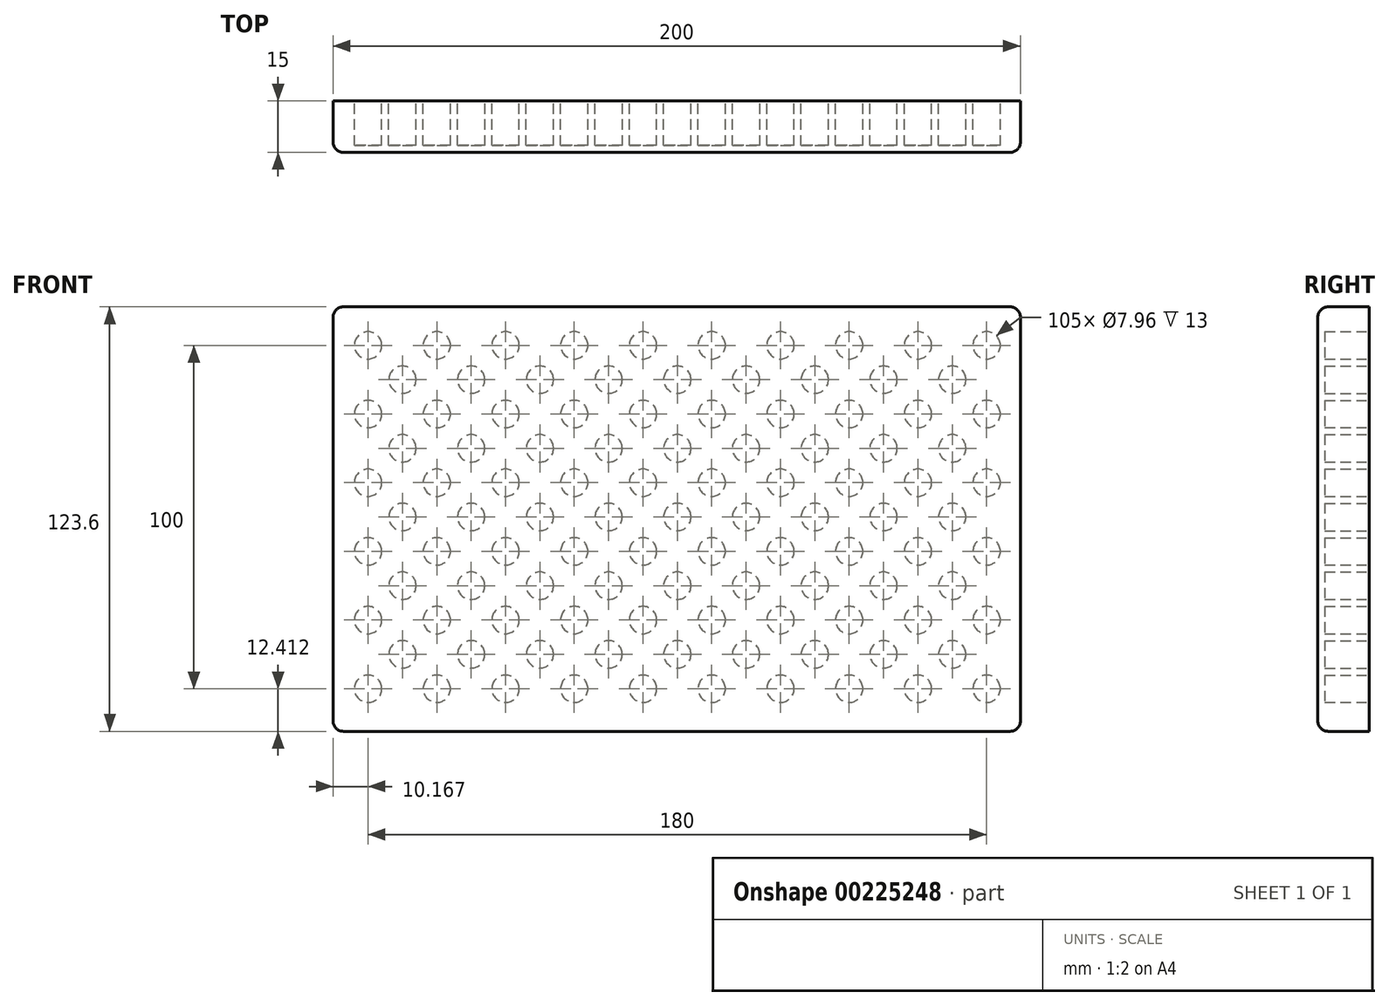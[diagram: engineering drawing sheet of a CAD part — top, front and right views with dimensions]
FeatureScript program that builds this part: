
annotation { "Feature Type Name" : "Feature", "Feature Type Description" : "" }
export const myFeature = defineFeature(function(context is Context, id is Id, definition is map)
    precondition{}
    {
        {
            var Q0;
            Q0=qCreatedBy(makeId("Front.planeOp"),FACE);
            var sketch = newSketch(context, id + "F0", { "sketchPlane" : qUnion([Q0])});
            skLineSegment(sketch, "E0.bottom", {"start": v(-100, 61.8) * mm, "end": v(23.6, 61.8) * mm});
            skLineSegment(sketch, "E0.top", {"start": v(-100, -61.8) * mm, "end": v(23.6, -61.8) * mm});
            skLineSegment(sketch, "E0.left", {"start": v(-100, 61.8) * mm, "end": v(-100, -61.8) * mm});
            skLineSegment(sketch, "E0.right", {"start": v(23.6, 61.8) * mm, "end": v(23.6, -61.8) * mm, "construction": true});
            skLineSegment(sketch, "E1", {"start": v(23.6, 61.8) * mm, "end": v(100, 61.8) * mm});
            skLineSegment(sketch, "E2", {"start": v(100, 61.8) * mm, "end": v(100, -61.8) * mm});
            skLineSegment(sketch, "E3", {"start": v(100, -61.8) * mm, "end": v(23.6, -61.8) * mm});
            skArc(sketch, "E4", {"start": v(23.6, 61.8) * mm, "mid": v(79.36, 10.85) * mm, "end": v(100, -61.8) * mm, "construction": true});
            skLineSegment(sketch, "E5", {"start": v(-38.2, -61.8) * mm, "end": v(23.6, 61.8) * mm, "construction": true});
            skSolve(sketch);
        }
        {
            var Q0;
            Q0=makeQuery(id+"F0.imprint","IMPRINT",FACE,{"disambiguationData":[TD([[makeQuery(id+"F0.imprint","IMPRINT",EDGE,{"derivedFrom":sQuery(id+"F0.wireOp",EDGE,"E0.bottom")}),-1.0]])]});
            extrude(context, id + "F1", {"entities" : qUnion([Q0]), "depth" : 15 * mm});
        }
        {
            var Q0;
            Q0=makeQuery(id+"F1.opExtrude","SWEPT_EDGE",EDGE,{"disambiguationData":[OSD([sQuery(id+"F0.wireOp",EDGE,"E0.bottom"),sQuery(id+"F0.wireOp",EDGE,"E0.left")])]});
            var Q1;
            Q1=makeQuery(id+"F1.opExtrude","SWEPT_EDGE",EDGE,{"disambiguationData":[OSD([sQuery(id+"F0.wireOp",EDGE,"E1"),sQuery(id+"F0.wireOp",EDGE,"E2")])]});
            var Q2;
            Q2=makeQuery(id+"F1.opExtrude","SWEPT_EDGE",EDGE,{"disambiguationData":[OSD([sQuery(id+"F0.wireOp",EDGE,"E0.top"),sQuery(id+"F0.wireOp",EDGE,"E0.left")])]});
            var Q3;
            Q3=makeQuery(id+"F1.opExtrude","SWEPT_EDGE",EDGE,{"disambiguationData":[OSD([sQuery(id+"F0.wireOp",EDGE,"E2"),sQuery(id+"F0.wireOp",EDGE,"E3")])]});
            var Q4;
            Q4=makeQuery(id+"F1.opExtrude","CAP_FACE",FACE,{"disambiguationData":[OSD([sQuery(id+"F0.wireOp",EDGE,"E0.bottom"),sQuery(id+"F0.wireOp",EDGE,"E0.top"),sQuery(id+"F0.wireOp",EDGE,"E0.left"),sQuery(id+"F0.wireOp",EDGE,"E1"),sQuery(id+"F0.wireOp",EDGE,"E2"),sQuery(id+"F0.wireOp",EDGE,"E3")])],"isStart":false});
            fillet(context, id + "F2", {"entities" : qUnion([Q0, Q1, Q2, Q3, Q4]), "radius" : 3 * mm, "tangentPropagation" : true, "allowEdgeOverflow" : false});
        }
        {
            var Q0;
            Q0=makeQuery(id+"F1.opExtrude","CAP_FACE",FACE,{"disambiguationData":[OSD([sQuery(id+"F0.wireOp",EDGE,"E0.bottom"),sQuery(id+"F0.wireOp",EDGE,"E0.top"),sQuery(id+"F0.wireOp",EDGE,"E0.left"),sQuery(id+"F0.wireOp",EDGE,"E1"),sQuery(id+"F0.wireOp",EDGE,"E2"),sQuery(id+"F0.wireOp",EDGE,"E3")])],"isStart":true});
            var sketch = newSketch(context, id + "F3", { "sketchPlane" : qUnion([Q0])});
            skLineSegment(sketch, "E6", {"start": v(85, 36.8) * mm, "end": v(-85, 36.8) * mm, "construction": true});
            skLineSegment(sketch, "E7", {"start": v(-65, 46.8) * mm, "end": v(-65, -46.8) * mm, "construction": true});
            skArc(sketch, "E8.0.startCap", {"start": v(85, 41.8) * mm, "mid": v(90, 36.8) * mm, "end": v(85, 31.8) * mm});
            skArc(sketch, "E8.0.endCap", {"start": v(-85, 31.8) * mm, "mid": v(-90, 36.8) * mm, "end": v(-85, 41.8) * mm});
            skLineSegment(sketch, "E8.0.left", {"start": v(85, 31.8) * mm, "end": v(-85, 31.8) * mm});
            skLineSegment(sketch, "E8.0.right", {"start": v(85, 41.8) * mm, "end": v(-85, 41.8) * mm});
            skArc(sketch, "E8.1.startCap", {"start": v(-70, 46.8) * mm, "mid": v(-65, 51.8) * mm, "end": v(-60, 46.8) * mm});
            skArc(sketch, "E8.1.endCap", {"start": v(-60, -46.8) * mm, "mid": v(-65, -51.8) * mm, "end": v(-70, -46.8) * mm});
            skLineSegment(sketch, "E8.1.left", {"start": v(-60, 46.8) * mm, "end": v(-60, -46.8) * mm});
            skLineSegment(sketch, "E8.1.right", {"start": v(-70, 46.8) * mm, "end": v(-70, -46.8) * mm});
            skSolve(sketch);
        }
        {
            var Q0;
            Q0=makeQuery(id+"F1.opExtrude","CAP_FACE",FACE,{"disambiguationData":[OSD([sQuery(id+"F0.wireOp",EDGE,"E0.bottom"),sQuery(id+"F0.wireOp",EDGE,"E0.top"),sQuery(id+"F0.wireOp",EDGE,"E0.left"),sQuery(id+"F0.wireOp",EDGE,"E1"),sQuery(id+"F0.wireOp",EDGE,"E2"),sQuery(id+"F0.wireOp",EDGE,"E3")])],"isStart":true});
            var sketch = newSketch(context, id + "F4", { "sketchPlane" : qUnion([Q0])});
            skLineSegment(sketch, "E9", {"start": v(75, 46.8) * mm, "end": v(-75, 46.8) * mm});
            skLineSegment(sketch, "E10", {"start": v(-85, 36.8) * mm, "end": v(-85, -36.8) * mm});
            skLineSegment(sketch, "E11", {"start": v(-75, -46.8) * mm, "end": v(-71, -46.8) * mm});
            skLineSegment(sketch, "E12", {"start": v(-61, -36.8) * mm, "end": v(-61, 22.8) * mm});
            skLineSegment(sketch, "E13", {"start": v(-61, 22.8) * mm, "end": v(75, 22.8) * mm});
            skLineSegment(sketch, "E14", {"start": v(85, 32.8) * mm, "end": v(85, 36.8) * mm});
            skLineSegment(sketch, "E15", {"start": v(85, 46.8) * mm, "end": v(100, 46.8) * mm, "construction": true});
            skLineSegment(sketch, "E16", {"start": v(-85, 46.8) * mm, "end": v(-85, 61.8) * mm, "construction": true});
            skLineSegment(sketch, "E17", {"start": v(-85, -46.8) * mm, "end": v(-85, -61.8) * mm, "construction": true});
            skLineSegment(sketch, "E18", {"start": v(-85, 46.8) * mm, "end": v(-100, 46.8) * mm, "construction": true});
            skPoint(sketch, "E19.visualSharp", {"position": v(-85, 46.8) * mm});
            skArc(sketch, "E19.filletArc", {"start": v(-75, 46.8) * mm, "mid": v(-82.07, 43.87) * mm, "end": v(-85, 36.8) * mm});
            skPoint(sketch, "E20.visualSharp", {"position": v(85, 46.8) * mm});
            skArc(sketch, "E20.filletArc", {"start": v(85, 36.8) * mm, "mid": v(82.07, 43.87) * mm, "end": v(75, 46.8) * mm});
            skPoint(sketch, "E21.visualSharp", {"position": v(85, 22.8) * mm});
            skArc(sketch, "E21.filletArc", {"start": v(75, 22.8) * mm, "mid": v(82.07, 25.73) * mm, "end": v(85, 32.8) * mm});
            skPoint(sketch, "E22.visualSharp", {"position": v(-61, -46.8) * mm});
            skArc(sketch, "E22.filletArc", {"start": v(-71, -46.8) * mm, "mid": v(-63.93, -43.87) * mm, "end": v(-61, -36.8) * mm});
            skPoint(sketch, "E23.visualSharp", {"position": v(-85, -46.8) * mm});
            skArc(sketch, "E23.filletArc", {"start": v(-85, -36.8) * mm, "mid": v(-82.07, -43.87) * mm, "end": v(-75, -46.8) * mm});
            skLineSegment(sketch, "E24", {"start": v(85, 22.8) * mm, "end": v(85, 46.8) * mm, "construction": true});
            skLineSegment(sketch, "E25", {"start": v(-61, -46.8) * mm, "end": v(-85, -46.8) * mm, "construction": true});
            skSolve(sketch);
        }
        {
            var Q0;
            Q0=makeQuery(id+"F1.opExtrude","CAP_FACE",FACE,{"disambiguationData":[OSD([sQuery(id+"F0.wireOp",EDGE,"E0.bottom"),sQuery(id+"F0.wireOp",EDGE,"E0.top"),sQuery(id+"F0.wireOp",EDGE,"E0.left"),sQuery(id+"F0.wireOp",EDGE,"E1"),sQuery(id+"F0.wireOp",EDGE,"E2"),sQuery(id+"F0.wireOp",EDGE,"E3")])],"isStart":true});
            var sketch = newSketch(context, id + "F5", { "sketchPlane" : qUnion([Q0])});
            skCircle(sketch, "E26", {"center": v(-90.17, 50.61) * mm, "radius": 3.98 * mm});
            skCircle(sketch, "E27.0.1.0", {"center": v(-90.17, 30.61) * mm, "radius": 3.98 * mm});
            skCircle(sketch, "E27.0.2.0", {"center": v(-90.17, 10.61) * mm, "radius": 3.98 * mm});
            skCircle(sketch, "E27.0.3.0", {"center": v(-90.17, -9.39) * mm, "radius": 3.98 * mm});
            skCircle(sketch, "E27.0.4.0", {"center": v(-90.17, -29.39) * mm, "radius": 3.98 * mm});
            skCircle(sketch, "E27.0.5.0", {"center": v(-90.17, -49.39) * mm, "radius": 3.98 * mm});
            skCircle(sketch, "E27.1.0.0", {"center": v(-70.17, 50.61) * mm, "radius": 3.98 * mm});
            skCircle(sketch, "E27.1.1.0", {"center": v(-70.17, 30.61) * mm, "radius": 3.98 * mm});
            skCircle(sketch, "E27.1.2.0", {"center": v(-70.17, 10.61) * mm, "radius": 3.98 * mm});
            skCircle(sketch, "E27.1.3.0", {"center": v(-70.17, -9.39) * mm, "radius": 3.98 * mm});
            skCircle(sketch, "E27.1.4.0", {"center": v(-70.17, -29.39) * mm, "radius": 3.98 * mm});
            skCircle(sketch, "E27.1.5.0", {"center": v(-70.17, -49.39) * mm, "radius": 3.98 * mm});
            skCircle(sketch, "E27.2.0.0", {"center": v(-50.17, 50.61) * mm, "radius": 3.98 * mm});
            skCircle(sketch, "E27.2.1.0", {"center": v(-50.17, 30.61) * mm, "radius": 3.98 * mm});
            skCircle(sketch, "E27.2.2.0", {"center": v(-50.17, 10.61) * mm, "radius": 3.98 * mm});
            skCircle(sketch, "E27.2.3.0", {"center": v(-50.17, -9.39) * mm, "radius": 3.98 * mm});
            skCircle(sketch, "E27.2.4.0", {"center": v(-50.17, -29.39) * mm, "radius": 3.98 * mm});
            skCircle(sketch, "E27.2.5.0", {"center": v(-50.17, -49.39) * mm, "radius": 3.98 * mm});
            skCircle(sketch, "E27.3.0.0", {"center": v(-30.17, 50.61) * mm, "radius": 3.98 * mm});
            skCircle(sketch, "E27.3.1.0", {"center": v(-30.17, 30.61) * mm, "radius": 3.98 * mm});
            skCircle(sketch, "E27.3.2.0", {"center": v(-30.17, 10.61) * mm, "radius": 3.98 * mm});
            skCircle(sketch, "E27.3.3.0", {"center": v(-30.17, -9.39) * mm, "radius": 3.98 * mm});
            skCircle(sketch, "E27.3.4.0", {"center": v(-30.17, -29.39) * mm, "radius": 3.98 * mm});
            skCircle(sketch, "E27.3.5.0", {"center": v(-30.17, -49.39) * mm, "radius": 3.98 * mm});
            skCircle(sketch, "E27.4.0.0", {"center": v(-10.17, 50.61) * mm, "radius": 3.98 * mm});
            skCircle(sketch, "E27.4.1.0", {"center": v(-10.17, 30.61) * mm, "radius": 3.98 * mm});
            skCircle(sketch, "E27.4.2.0", {"center": v(-10.17, 10.61) * mm, "radius": 3.98 * mm});
            skCircle(sketch, "E27.4.3.0", {"center": v(-10.17, -9.39) * mm, "radius": 3.98 * mm});
            skCircle(sketch, "E27.4.4.0", {"center": v(-10.17, -29.39) * mm, "radius": 3.98 * mm});
            skCircle(sketch, "E27.4.5.0", {"center": v(-10.17, -49.39) * mm, "radius": 3.98 * mm});
            skCircle(sketch, "E27.5.0.0", {"center": v(9.83, 50.61) * mm, "radius": 3.98 * mm});
            skCircle(sketch, "E27.5.1.0", {"center": v(9.83, 30.61) * mm, "radius": 3.98 * mm});
            skCircle(sketch, "E27.5.2.0", {"center": v(9.83, 10.61) * mm, "radius": 3.98 * mm});
            skCircle(sketch, "E27.5.3.0", {"center": v(9.83, -9.39) * mm, "radius": 3.98 * mm});
            skCircle(sketch, "E27.5.4.0", {"center": v(9.83, -29.39) * mm, "radius": 3.98 * mm});
            skCircle(sketch, "E27.5.5.0", {"center": v(9.83, -49.39) * mm, "radius": 3.98 * mm});
            skCircle(sketch, "E27.6.0.0", {"center": v(29.83, 50.61) * mm, "radius": 3.98 * mm});
            skCircle(sketch, "E27.6.1.0", {"center": v(29.83, 30.61) * mm, "radius": 3.98 * mm});
            skCircle(sketch, "E27.6.2.0", {"center": v(29.83, 10.61) * mm, "radius": 3.98 * mm});
            skCircle(sketch, "E27.6.3.0", {"center": v(29.83, -9.39) * mm, "radius": 3.98 * mm});
            skCircle(sketch, "E27.6.4.0", {"center": v(29.83, -29.39) * mm, "radius": 3.98 * mm});
            skCircle(sketch, "E27.6.5.0", {"center": v(29.83, -49.39) * mm, "radius": 3.98 * mm});
            skCircle(sketch, "E27.7.0.0", {"center": v(49.83, 50.61) * mm, "radius": 3.98 * mm});
            skCircle(sketch, "E27.7.1.0", {"center": v(49.83, 30.61) * mm, "radius": 3.98 * mm});
            skCircle(sketch, "E27.7.2.0", {"center": v(49.83, 10.61) * mm, "radius": 3.98 * mm});
            skCircle(sketch, "E27.7.3.0", {"center": v(49.83, -9.39) * mm, "radius": 3.98 * mm});
            skCircle(sketch, "E27.7.4.0", {"center": v(49.83, -29.39) * mm, "radius": 3.98 * mm});
            skCircle(sketch, "E27.7.5.0", {"center": v(49.83, -49.39) * mm, "radius": 3.98 * mm});
            skCircle(sketch, "E27.8.0.0", {"center": v(69.83, 50.61) * mm, "radius": 3.98 * mm});
            skCircle(sketch, "E27.8.1.0", {"center": v(69.83, 30.61) * mm, "radius": 3.98 * mm});
            skCircle(sketch, "E27.8.2.0", {"center": v(69.83, 10.61) * mm, "radius": 3.98 * mm});
            skCircle(sketch, "E27.8.3.0", {"center": v(69.83, -9.39) * mm, "radius": 3.98 * mm});
            skCircle(sketch, "E27.8.4.0", {"center": v(69.83, -29.39) * mm, "radius": 3.98 * mm});
            skCircle(sketch, "E27.8.5.0", {"center": v(69.83, -49.39) * mm, "radius": 3.98 * mm});
            skCircle(sketch, "E27.9.0.0", {"center": v(89.83, 50.61) * mm, "radius": 3.98 * mm});
            skCircle(sketch, "E27.9.1.0", {"center": v(89.83, 30.61) * mm, "radius": 3.98 * mm});
            skCircle(sketch, "E27.9.2.0", {"center": v(89.83, 10.61) * mm, "radius": 3.98 * mm});
            skCircle(sketch, "E27.9.3.0", {"center": v(89.83, -9.39) * mm, "radius": 3.98 * mm});
            skCircle(sketch, "E27.9.4.0", {"center": v(89.83, -29.39) * mm, "radius": 3.98 * mm});
            skCircle(sketch, "E27.9.5.0", {"center": v(89.83, -49.39) * mm, "radius": 3.98 * mm});
            skLineSegment(sketch, "E27.direction1", {"start": v(-90.17, 50.61) * mm, "end": v(-70.17, 50.61) * mm, "construction": true});
            skLineSegment(sketch, "E27.direction2", {"start": v(-90.17, 50.61) * mm, "end": v(-90.17, 30.61) * mm, "construction": true});
            skLineSegment(sketch, "E28", {"start": v(-70.17, 30.61) * mm, "end": v(-90.17, 50.61) * mm, "construction": true});
            skCircle(sketch, "E29", {"center": v(-80.17, 40.61) * mm, "radius": 3.98 * mm});
            skCircle(sketch, "E30.0.1.0", {"center": v(-80.17, 20.61) * mm, "radius": 3.98 * mm});
            skCircle(sketch, "E30.0.2.0", {"center": v(-80.17, 0.61) * mm, "radius": 3.98 * mm});
            skCircle(sketch, "E30.0.3.0", {"center": v(-80.17, -19.39) * mm, "radius": 3.98 * mm});
            skCircle(sketch, "E30.0.4.0", {"center": v(-80.17, -39.39) * mm, "radius": 3.98 * mm});
            skCircle(sketch, "E30.1.0.0", {"center": v(-60.17, 40.61) * mm, "radius": 3.98 * mm});
            skCircle(sketch, "E30.1.1.0", {"center": v(-60.17, 20.61) * mm, "radius": 3.98 * mm});
            skCircle(sketch, "E30.1.2.0", {"center": v(-60.17, 0.61) * mm, "radius": 3.98 * mm});
            skCircle(sketch, "E30.1.3.0", {"center": v(-60.17, -19.39) * mm, "radius": 3.98 * mm});
            skCircle(sketch, "E30.1.4.0", {"center": v(-60.17, -39.39) * mm, "radius": 3.98 * mm});
            skCircle(sketch, "E30.2.0.0", {"center": v(-40.17, 40.61) * mm, "radius": 3.98 * mm});
            skCircle(sketch, "E30.2.1.0", {"center": v(-40.17, 20.61) * mm, "radius": 3.98 * mm});
            skCircle(sketch, "E30.2.2.0", {"center": v(-40.17, 0.61) * mm, "radius": 3.98 * mm});
            skCircle(sketch, "E30.2.3.0", {"center": v(-40.17, -19.39) * mm, "radius": 3.98 * mm});
            skCircle(sketch, "E30.2.4.0", {"center": v(-40.17, -39.39) * mm, "radius": 3.98 * mm});
            skCircle(sketch, "E30.3.0.0", {"center": v(-20.17, 40.61) * mm, "radius": 3.98 * mm});
            skCircle(sketch, "E30.3.1.0", {"center": v(-20.17, 20.61) * mm, "radius": 3.98 * mm});
            skCircle(sketch, "E30.3.2.0", {"center": v(-20.17, 0.61) * mm, "radius": 3.98 * mm});
            skCircle(sketch, "E30.3.3.0", {"center": v(-20.17, -19.39) * mm, "radius": 3.98 * mm});
            skCircle(sketch, "E30.3.4.0", {"center": v(-20.17, -39.39) * mm, "radius": 3.98 * mm});
            skCircle(sketch, "E30.4.0.0", {"center": v(-0.17, 40.61) * mm, "radius": 3.98 * mm});
            skCircle(sketch, "E30.4.1.0", {"center": v(-0.17, 20.61) * mm, "radius": 3.98 * mm});
            skCircle(sketch, "E30.4.2.0", {"center": v(-0.17, 0.61) * mm, "radius": 3.98 * mm});
            skCircle(sketch, "E30.4.3.0", {"center": v(-0.17, -19.39) * mm, "radius": 3.98 * mm});
            skCircle(sketch, "E30.4.4.0", {"center": v(-0.17, -39.39) * mm, "radius": 3.98 * mm});
            skCircle(sketch, "E30.5.0.0", {"center": v(19.83, 40.61) * mm, "radius": 3.98 * mm});
            skCircle(sketch, "E30.5.1.0", {"center": v(19.83, 20.61) * mm, "radius": 3.98 * mm});
            skCircle(sketch, "E30.5.2.0", {"center": v(19.83, 0.61) * mm, "radius": 3.98 * mm});
            skCircle(sketch, "E30.5.3.0", {"center": v(19.83, -19.39) * mm, "radius": 3.98 * mm});
            skCircle(sketch, "E30.5.4.0", {"center": v(19.83, -39.39) * mm, "radius": 3.98 * mm});
            skCircle(sketch, "E30.6.0.0", {"center": v(39.83, 40.61) * mm, "radius": 3.98 * mm});
            skCircle(sketch, "E30.6.1.0", {"center": v(39.83, 20.61) * mm, "radius": 3.98 * mm});
            skCircle(sketch, "E30.6.2.0", {"center": v(39.83, 0.61) * mm, "radius": 3.98 * mm});
            skCircle(sketch, "E30.6.3.0", {"center": v(39.83, -19.39) * mm, "radius": 3.98 * mm});
            skCircle(sketch, "E30.6.4.0", {"center": v(39.83, -39.39) * mm, "radius": 3.98 * mm});
            skCircle(sketch, "E30.7.0.0", {"center": v(59.83, 40.61) * mm, "radius": 3.98 * mm});
            skCircle(sketch, "E30.7.1.0", {"center": v(59.83, 20.61) * mm, "radius": 3.98 * mm});
            skCircle(sketch, "E30.7.2.0", {"center": v(59.83, 0.61) * mm, "radius": 3.98 * mm});
            skCircle(sketch, "E30.7.3.0", {"center": v(59.83, -19.39) * mm, "radius": 3.98 * mm});
            skCircle(sketch, "E30.7.4.0", {"center": v(59.83, -39.39) * mm, "radius": 3.98 * mm});
            skCircle(sketch, "E30.8.0.0", {"center": v(79.83, 40.61) * mm, "radius": 3.98 * mm});
            skCircle(sketch, "E30.8.1.0", {"center": v(79.83, 20.61) * mm, "radius": 3.98 * mm});
            skCircle(sketch, "E30.8.2.0", {"center": v(79.83, 0.61) * mm, "radius": 3.98 * mm});
            skCircle(sketch, "E30.8.3.0", {"center": v(79.83, -19.39) * mm, "radius": 3.98 * mm});
            skCircle(sketch, "E30.8.4.0", {"center": v(79.83, -39.39) * mm, "radius": 3.98 * mm});
            skLineSegment(sketch, "E30.direction1", {"start": v(-80.17, 40.61) * mm, "end": v(-60.17, 40.61) * mm, "construction": true});
            skLineSegment(sketch, "E30.direction2", {"start": v(-80.17, 40.61) * mm, "end": v(-80.17, 20.61) * mm, "construction": true});
            skSolve(sketch);
        }
        {
            var Q0;
            Q0 = qSketchRegion(id + "F5", true);
            extrude(context, id + "F6", {"entities" : qUnion([Q0]), "operationType" : NewBodyOperationType.REMOVE, "oppositeDirection" : true, "depth" : (15 - 2) * mm});
        }
    });
